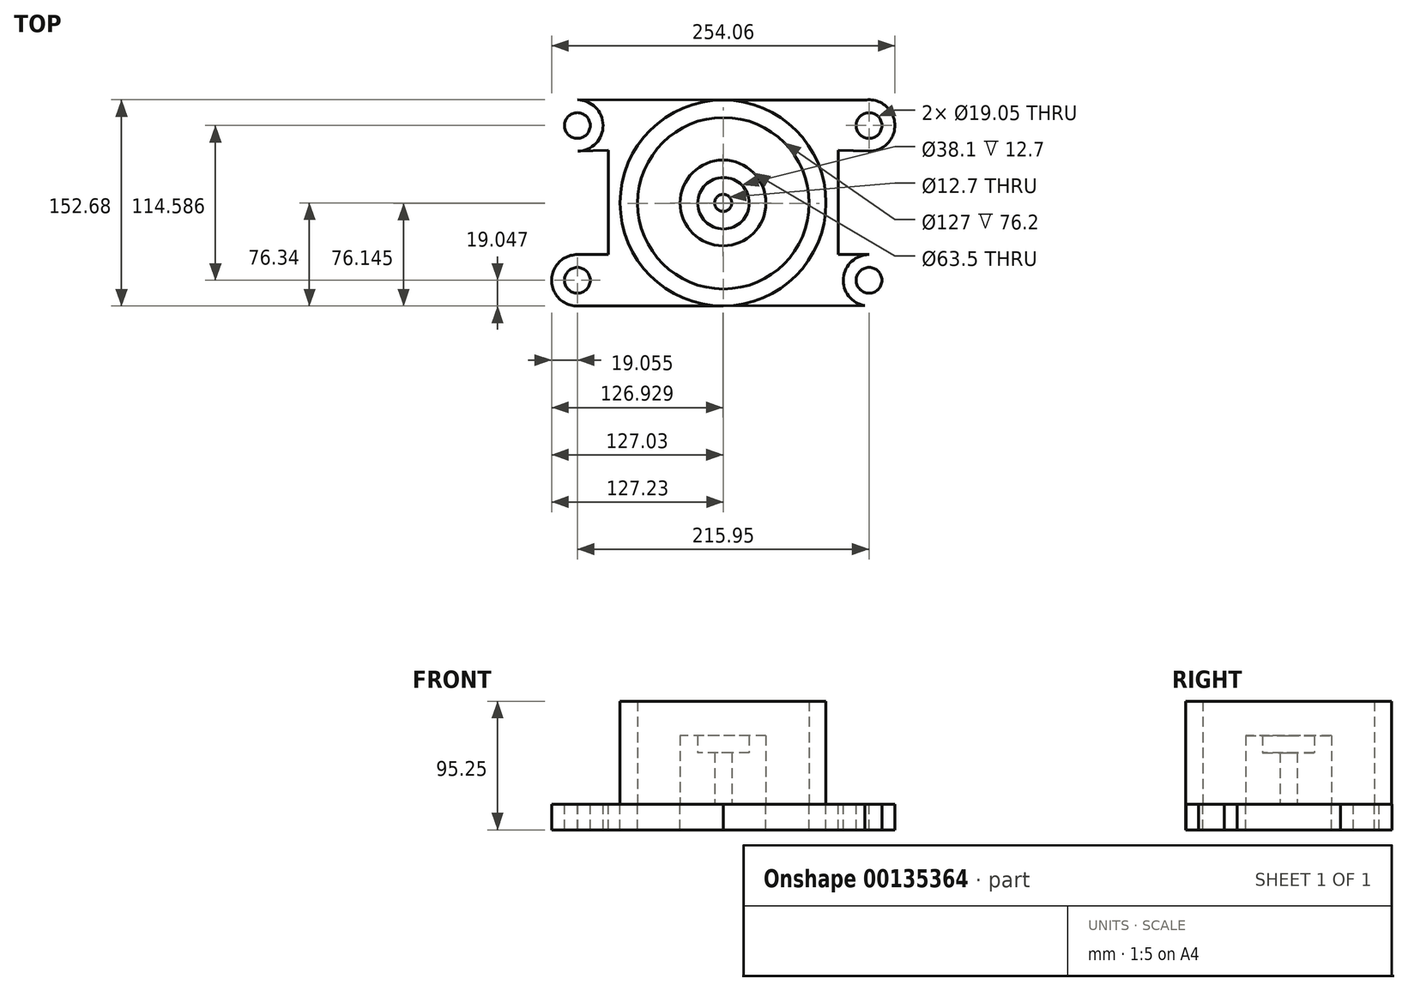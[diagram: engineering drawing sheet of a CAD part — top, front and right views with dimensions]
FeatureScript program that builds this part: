
annotation { "Feature Type Name" : "Feature", "Feature Type Description" : "" }
export const myFeature = defineFeature(function(context is Context, id is Id, definition is map)
    precondition{}
    {
        {
            var Q0;
            Q0=qCreatedBy(makeId("Top.planeOp"),FACE);
            var sketch = newSketch(context, id + "F0", { "sketchPlane" : qUnion([Q0])});
            skCircle(sketch, "E0", {"center": v(0, 0) * mm, "radius": 6.35 * mm});
            skCircle(sketch, "E1", {"center": v(-0.1, 0) * mm, "radius": 31.75 * mm});
            skCircle(sketch, "E2", {"center": v(0.2, -0.2) * mm, "radius": 19.05 * mm});
            skCircle(sketch, "E3", {"center": v(0.2, -0.2) * mm, "radius": 63.5 * mm});
            skCircle(sketch, "E4", {"center": v(-0.1, 0) * mm, "radius": 76.2 * mm});
            skLineSegment(sketch, "E5", {"start": v(0, -76.2) * mm, "end": v(107.95, -76.06) * mm});
            skLineSegment(sketch, "E6", {"start": v(0, -76.2) * mm, "end": v(-107.95, -76.34) * mm});
            skLineSegment(sketch, "E7", {"start": v(-107.95, -76.34) * mm, "end": v(-108, -38.24) * mm, "construction": true});
            skCircle(sketch, "E8", {"center": v(-107.98, -57.3) * mm, "radius": 19.05 * mm});
            skCircle(sketch, "E9", {"center": v(-107.98, -57.3) * mm, "radius": 9.53 * mm});
            skCircle(sketch, "E10.MirrorC", {"center": v(-107.98, 57.3) * mm, "radius": 19.05 * mm});
            skCircle(sketch, "E11.MirrorC", {"center": v(-107.98, 57.3) * mm, "radius": 9.53 * mm});
            skLineSegment(sketch, "E12.MirrorCS", {"start": v(0, 76.2) * mm, "end": v(-107.95, 76.34) * mm});
            skLineSegment(sketch, "E13.MirrorCS", {"start": v(0, 76.2) * mm, "end": v(107.95, 76.06) * mm});
            skCircle(sketch, "E14.MirrorC", {"center": v(107.98, -57.3) * mm, "radius": 19.05 * mm});
            skCircle(sketch, "E15.MirrorC", {"center": v(107.98, -57.3) * mm, "radius": 9.53 * mm});
            skCircle(sketch, "E16.MirrorC", {"center": v(107.98, 57.3) * mm, "radius": 19.05 * mm});
            skCircle(sketch, "E17.MirrorC", {"center": v(107.98, 57.3) * mm, "radius": 9.53 * mm});
            skLineSegment(sketch, "E18", {"start": v(-108, -38.24) * mm, "end": v(-85.02, -38.21) * mm});
            skLineSegment(sketch, "E19", {"start": v(-85.02, -38.21) * mm, "end": v(-85.12, 38.87) * mm});
            skLineSegment(sketch, "E20", {"start": v(-85.12, 38.87) * mm, "end": v(-107.45, 38.25) * mm});
            skLineSegment(sketch, "E21.MirrorCS", {"start": v(85.12, 38.87) * mm, "end": v(107.45, 38.25) * mm});
            skLineSegment(sketch, "E22.MirrorCS", {"start": v(85.02, -38.21) * mm, "end": v(85.12, 38.87) * mm});
            skLineSegment(sketch, "E23.MirrorCS", {"start": v(108, -38.24) * mm, "end": v(85.02, -38.21) * mm});
            skSolve(sketch);
        }
        {
            var Q0;
            Q0=makeQuery(id+"F0.imprint","IMPRINT",FACE,{"disambiguationData":[TD([[makeQuery(id+"F0.imprint","IMPRINT",EDGE,{"derivedFrom":sQuery(id+"F0.wireOp",EDGE,"E11.MirrorC")}),1.0]])]});
            var Q1;
            Q1=makeQuery(id+"F0.imprint","IMPRINT",FACE,{"disambiguationData":[TD([[makeQuery(id+"F0.imprint","IMPRINT",EDGE,{"derivedFrom":sQuery(id+"F0.wireOp",EDGE,"E9")}),-1.0]])]});
            var Q2;
            Q2=makeQuery(id+"F0.imprint","IMPRINT",FACE,{"disambiguationData":[TD([[makeQuery(id+"F0.imprint","IMPRINT",EDGE,{"derivedFrom":sQuery(id+"F0.wireOp",EDGE,"E17.MirrorC")}),-1.0]])]});
            var Q3;
            Q3=makeQuery(id+"F0.imprint","IMPRINT",FACE,{"disambiguationData":[TD([[makeQuery(id+"F0.imprint","IMPRINT",EDGE,{"derivedFrom":sQuery(id+"F0.wireOp",EDGE,"E15.MirrorC")}),1.0]])]});
            var Q4;
            Q4=makeQuery(id+"F0.imprint","IMPRINT",FACE,{"disambiguationData":[TD([[makeQuery(id+"F0.imprint","IMPRINT",EDGE,{"derivedFrom":sQuery(id+"F0.wireOp",EDGE,"E1")}),-1.0]])]});
            var Q5;
            {var subQ10=sQuery(id+"F0.wireOp",EDGE,"E21.MirrorCS");Q5=makeQuery(id+"F0.imprint","IMPRINT",FACE,{"disambiguationData":[TD([[makeQuery(id+"F0.imprint","IMPRINT",EDGE,{"derivedFrom":subQ10}),1.0]])]});}
            var Q6;
            {var subQ4=sQuery(id+"F0.wireOp",EDGE,"E6");Q6=makeQuery(id+"F0.imprint","IMPRINT",FACE,{"disambiguationData":[TD([[makeQuery(id+"F0.imprint","IMPRINT",EDGE,{"derivedFrom":subQ4}),-1.0]])]});}
            extrude(context, id + "F1", {"entities" : qUnion([Q0, Q1, Q2, Q3, Q4, Q5, Q6]), "oppositeDirection" : true, "depth" : 19.05 * mm});
        }
        {
            var Q0;
            Q0=makeQuery(id+"F0.imprint","IMPRINT",FACE,{"disambiguationData":[TD([[makeQuery(id+"F0.imprint","IMPRINT",EDGE,{"derivedFrom":sQuery(id+"F0.wireOp",EDGE,"E1")}),1.0]])]});
            extrude(context, id + "F2", {"entities" : qUnion([Q0]), "depth" : 50.8 * mm});
        }
        {
            var Q0;
            Q0=makeQuery(id+"F0.imprint","IMPRINT",FACE,{"disambiguationData":[TD([[makeQuery(id+"F0.imprint","IMPRINT",EDGE,{"derivedFrom":sQuery(id+"F0.wireOp",EDGE,"E3")}),-1.0]])]});
            extrude(context, id + "F3", {"entities" : qUnion([Q0]), "depth" : 76.2 * mm});
        }
        {
            var Q0;
            Q0=makeQuery(id+"F0.imprint","IMPRINT",FACE,{"disambiguationData":[TD([[makeQuery(id+"F0.imprint","IMPRINT",EDGE,{"derivedFrom":sQuery(id+"F0.wireOp",EDGE,"E0")}),-1.0]])]});
            extrude(context, id + "F4", {"entities" : qUnion([Q0]), "operationType" : NewBodyOperationType.ADD, "depth" : 38.1 * mm});
        }
    });
